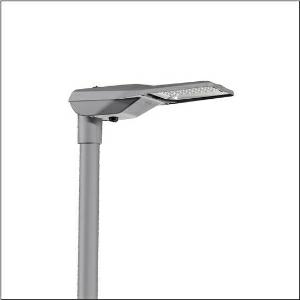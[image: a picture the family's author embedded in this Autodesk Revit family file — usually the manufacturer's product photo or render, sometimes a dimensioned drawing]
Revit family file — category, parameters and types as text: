
# Revit family: streetlight_sl_21_iq_mini___p0_8a_5xe2u31y08gb_4fe4
name_source: partatom
category: Lighting Fixtures
units: mm (PartAtom-declared; Revit-internal decimal feet)

## family parameters
Cut with Voids When Loaded = No
Host = Face
Light Source = No
Part Type = Normal
Room Calculation Point = No
Round Connector Dimension = Use Diameter
Shared = No

## types (1)
- --- (1 x LED, 6040 lm, 39.8 W, 3000K)
    Apparent Load = 40 VA
    CIE Flux Codes = 33 69 96 100 100
    Color Rendering = 70
    Color Temperature = 3000K
    Default Elevation = 1800 mm
    Description = Streetlight SL 21 iQ mini, mast luminaire, primary light control with lens, of PMMA, primary optical cover: cover, of toughened safety glass, transparent, light distribution: P0.8a, light emission: direct distribution, primary light characteristic: asymmetric, installation type: post-top, side-entry, LED, High Power LED, rated luminous flux: 6.040lm, luminous efficacy: 152lm/W, light colour: 730, colour temperature: 3000K, control gear: iQ-Street Remote, D4i with power reduction, control: pre-setting: logarithmic dimming characteristic, Street-Remote, Auto-Match, Temp-Guard, Lumen-Switch, Night-Set, Smart-Wire, Light-Fading, Desk-Remote (wireless, voltage-free reading and setting of iQ features in the workshop via application-optimized NFC function/RFID function), optimised constant luminous flux control (CLO 2.0), mains connection: 220..240V, AC, 50/60Hz, start of lifetime: 40W, end of service life: 41W, reduction: 18W, luminaire housing, of diecast aluminium, powder-coated, SITECO metallic grey (DB 702S), corrosivity category C5 high according to DIN EN ISO 12944, please order mast flange separately, inclination adjustable: 0°, 5°, 10°, 15°, sealing non-destructively replaceable, multi-level sealing system, length: 628mm, width: 235mm, height: 110mm, mast flange for spigot size: 42mm (side-entry): 5XC10008XM4, 60/48mm (side-entry/post-top): 5XC10108XM2, 76/60mm (side-entry/post-top): 5XC10108XM1, mounting height: 4..8m, Smart Interface below and above, protection rating (complete): IP66, insulation class (complete): insulation class II (safety insulation), certification: CE, ENEC, ENEC+, VDE, impact resistance: IK10, permissible operating ambient temperature for outdoor applications: -40..+50°C, standard-compliant lighting for roads and squares, packaging unit: 1 piece

Light Distribution: P0.8a
    Height = 110 mm
    Lamp = 1 x LED
    Lamp Light Flux = 6040 lm
    Lamp Power = 39.8 W
    Lamp count = 1
    Length = 625 mm
    Luminous efficacy = 152 lm/W
    Manufacturer = Siteco
    ModVariant = No
    Model = 5XE2U31Y08GB
    Number of Poles = 1
    OnlyDefault = Yes
    Power Factor = 1
    Product Name = Streetlight SL 21 iQ mini | P0.8a
    Product group = mast luminaire | pylon top
    ProductGroupID = 6100
    Protection Class = Protection class II
    Protection Degree = IP 66
    RLX_Detail_Level = 1
    RLX_Emergency_Light_Flux = 0 lm
    RLX_Emergency_Type = 0
    RLX_Emergency_Type_DB = No
    RlxData = <blob elided: 93301 chars, md5=368883ae>
    Socket = socket
    Standby Power = 0 W
    System Light Flux = 6040 lm
    System Power = 40 W
    Type Comments = factory setting: luminous flux: 100 % | dim-lin: 254 | 800 mA
    Type Image = l_1003514.jpg
    URL = http://relux.com
    VarID = @adj_081801
    Voltage = 0 V
    Weight = 0.00 kg
    Width = 234 mm

## geometry (parser evidence)
native form markers: Blend x4, Sweep x10
no freeform markers — native parametric forms only
